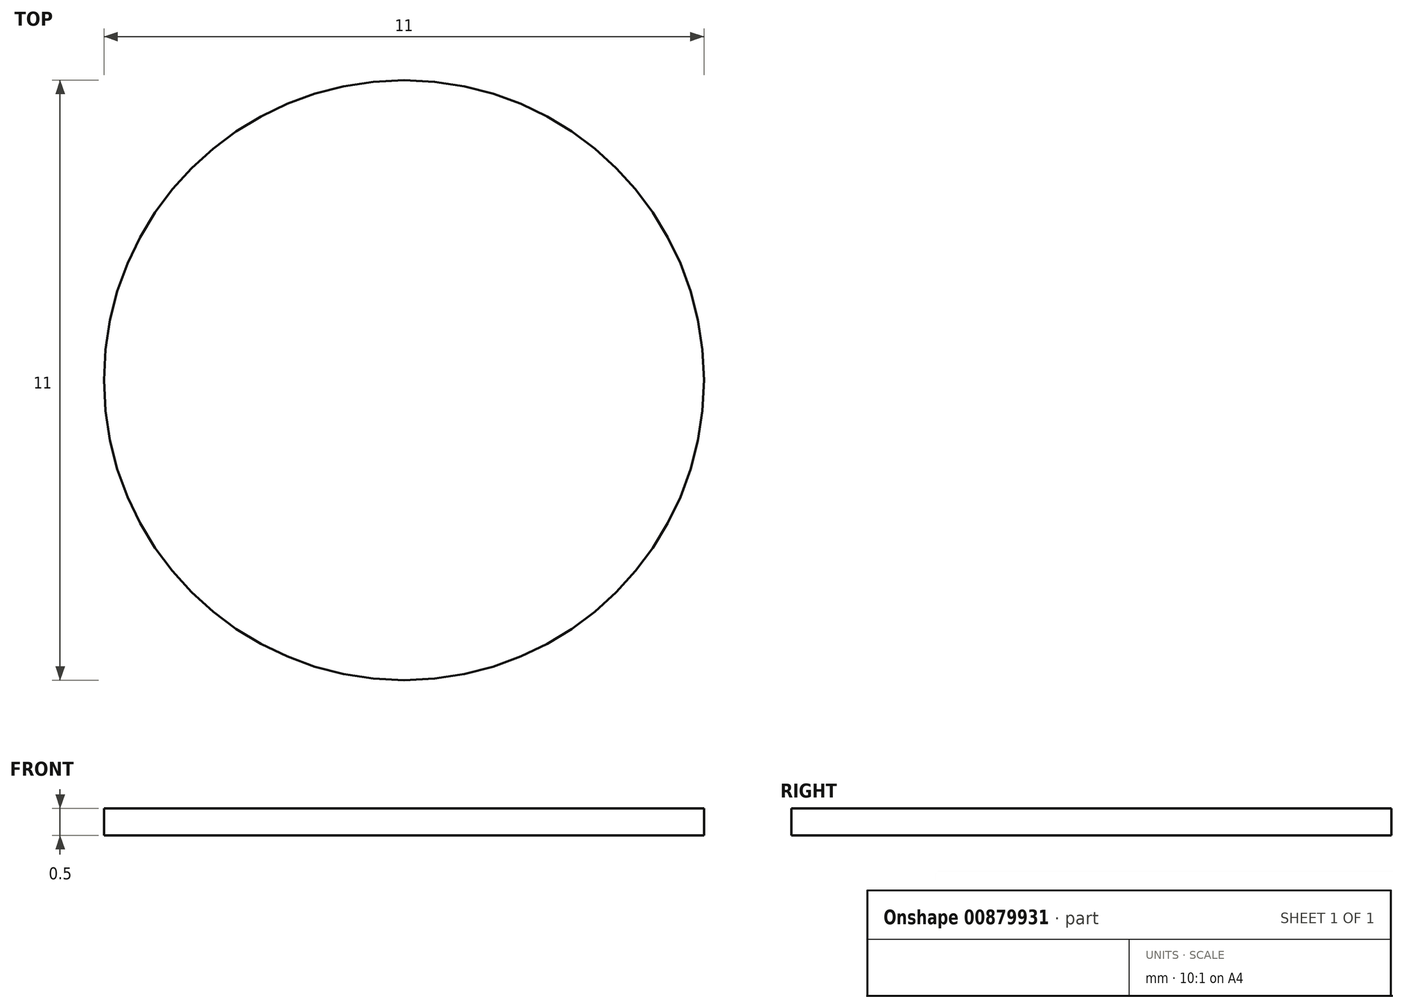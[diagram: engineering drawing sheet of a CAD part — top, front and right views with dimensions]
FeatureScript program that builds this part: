
annotation { "Feature Type Name" : "Feature", "Feature Type Description" : "" }
export const myFeature = defineFeature(function(context is Context, id is Id, definition is map)
    precondition{}
    {
        {
            var Q0;
            Q0=qCreatedBy(makeId("Top.planeOp"),FACE);
            var sketch = newSketch(context, id + "F0", { "sketchPlane" : qUnion([Q0])});
            skCircle(sketch, "E0", {"center": v(0, 0) * mm, "radius": 5.5 * mm});
            skSolve(sketch);
        }
        {
            var Q0;
            Q0=makeQuery(id+"F0.imprint","IMPRINT",FACE,{"disambiguationData":[TD([[makeQuery(id+"F0.imprint","IMPRINT",EDGE,{"derivedFrom":sQuery(id+"F0.wireOp",EDGE,"E0")}),1.0]])]});
            extrude(context, id + "F1", {"entities" : qUnion([Q0]), "depth" : 0.5 * mm, "offsetDistance" : 25 * mm});
        }
    });
